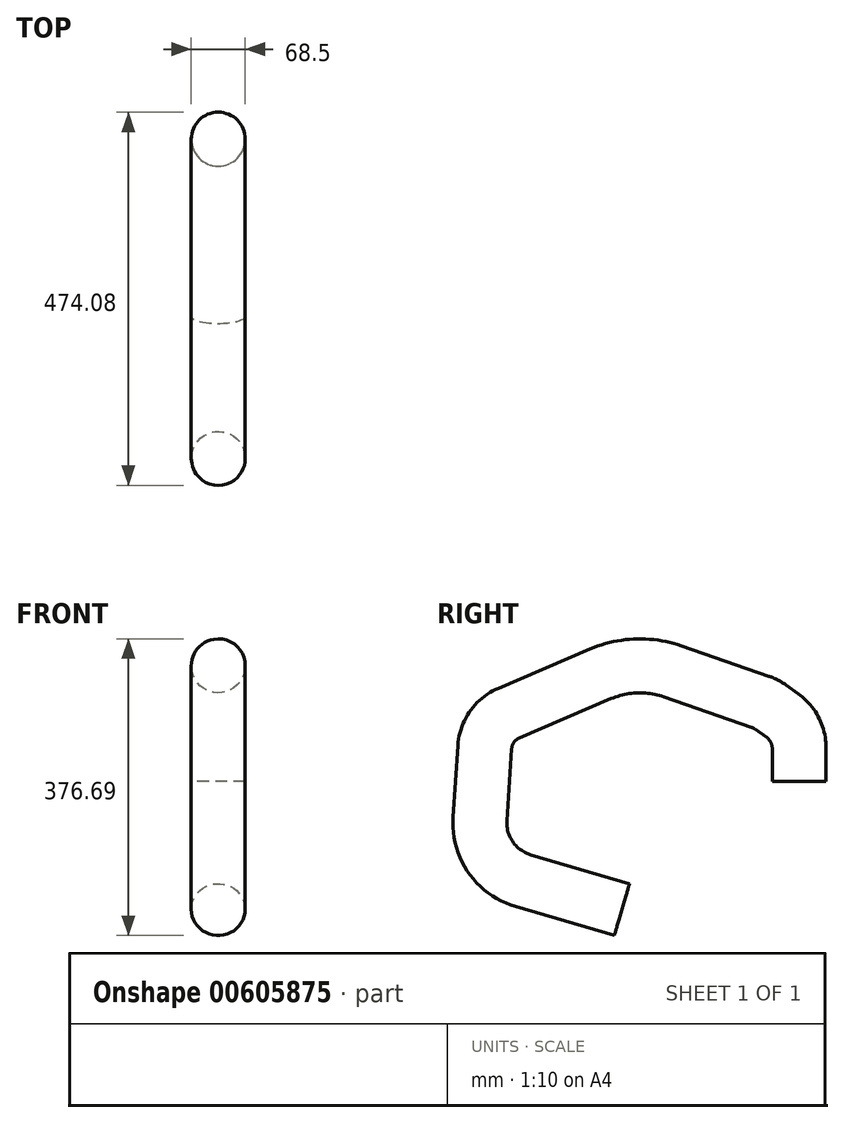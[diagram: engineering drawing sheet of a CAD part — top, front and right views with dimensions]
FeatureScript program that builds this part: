
annotation { "Feature Type Name" : "Feature", "Feature Type Description" : "" }
export const myFeature = defineFeature(function(context is Context, id is Id, definition is map)
    precondition{}
    {
        {
            var Q0;
            Q0=qCreatedBy(makeId("Top.planeOp"),FACE);
            var sketch = newSketch(context, id + "F0", { "sketchPlane" : qUnion([Q0])});
            skCircle(sketch, "E0", {"center": v(0, 0) * mm, "radius": 34.25 * mm});
            skSolve(sketch);
        }
        {
            var Q0;
            Q0=qCreatedBy(makeId("Right.planeOp"),FACE);
            var sketch = newSketch(context, id + "F1", { "sketchPlane" : qUnion([Q0])});
            skLineSegment(sketch, "E1", {"start": v(0, 0) * mm, "end": v(0, 42.1) * mm});
            skLineSegment(sketch, "E2", {"start": v(-21.2, 83.38) * mm, "end": v(-36.53, 94.39) * mm});
            skLineSegment(sketch, "E3", {"start": v(-49.48, 101.1) * mm, "end": v(-160.72, 139.7) * mm});
            skLineSegment(sketch, "E4", {"start": v(-252.25, 136.52) * mm, "end": v(-368.7, 86.78) * mm});
            skLineSegment(sketch, "E5", {"start": v(-399.43, 43.39) * mm, "end": v(-405.42, -47.91) * mm});
            skLineSegment(sketch, "E6", {"start": v(-350.8, -126.03) * mm, "end": v(-225.1, -162.86) * mm});
            skArc(sketch, "E7.filletArc", {"start": v(0, 42.1) * mm, "mid": v(-5.6, 65.3) * mm, "end": v(-21.2, 83.38) * mm});
            skPoint(sketch, "E8.visualSharp", {"position": v(-42.52, 98.68) * mm});
            skArc(sketch, "E8.filletArc", {"start": v(-36.53, 94.39) * mm, "mid": v(-42.76, 98.21) * mm, "end": v(-49.48, 101.1) * mm});
            skPoint(sketch, "E9.visualSharp", {"position": v(-207.1, 155.8) * mm});
            skArc(sketch, "E9.filletArc", {"start": v(-160.72, 139.7) * mm, "mid": v(-206.79, 146.65) * mm, "end": v(-252.25, 136.52) * mm});
            skPoint(sketch, "E10.visualSharp", {"position": v(-397.38, 74.52) * mm});
            skArc(sketch, "E10.filletArc", {"start": v(-368.7, 86.78) * mm, "mid": v(-390.19, 69.42) * mm, "end": v(-399.43, 43.39) * mm});
            skPoint(sketch, "E11.visualSharp", {"position": v(-409.43, -108.86) * mm});
            skArc(sketch, "E11.filletArc", {"start": v(-405.42, -47.91) * mm, "mid": v(-391.84, -96.57) * mm, "end": v(-350.8, -126.03) * mm});
            skSolve(sketch);
        }
        {
            var Q0;
            Q0=makeQuery(id+"F0.imprint","IMPRINT",FACE,{"disambiguationData":[TD([[makeQuery(id+"F0.imprint","IMPRINT",EDGE,{"derivedFrom":sQuery(id+"F0.wireOp",EDGE,"E0")}),1.0]])]});
            var Q1;
            Q1=sQuery(id+"F1.wireOp",EDGE,"E2");
            var Q2;
            Q2=sQuery(id+"F1.wireOp",EDGE,"E1");
            var Q3;
            Q3=sQuery(id+"F1.wireOp",EDGE,"E3");
            var Q4;
            Q4=sQuery(id+"F1.wireOp",EDGE,"E4");
            var Q5;
            Q5=sQuery(id+"F1.wireOp",EDGE,"E5");
            var Q6;
            Q6=sQuery(id+"F1.wireOp",EDGE,"E6");
            var Q7;
            Q7=sQuery(id+"F1.wireOp",EDGE,"E7.filletArc");
            var Q8;
            Q8=sQuery(id+"F1.wireOp",EDGE,"E8.filletArc");
            var Q9;
            Q9=sQuery(id+"F1.wireOp",EDGE,"E9.filletArc");
            var Q10;
            Q10=sQuery(id+"F1.wireOp",EDGE,"E10.filletArc");
            var Q11;
            Q11=sQuery(id+"F1.wireOp",EDGE,"E11.filletArc");
            sweep(context, id + "F2", {"profiles" : qUnion([Q0]), "path" : qUnion([Q1, Q2, Q3, Q4, Q5, Q6, Q7, Q8, Q9, Q10, Q11])});
        }
    });
